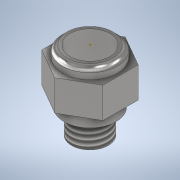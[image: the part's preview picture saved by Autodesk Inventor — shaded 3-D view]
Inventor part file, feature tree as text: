
AUTODESK INVENTOR PART (.ipt)
format: ipt  version: 2022 (Build 260153000, 153)  size: 174,592 bytes
history: native  units: mm
features: sketch x7, extrude x6, fillet x1, thread x1
ambient origin geometry x8: Origin, YZ Plane, XZ Plane, XY Plane, X Axis, Y Axis, Z Axis, Center Point
bodies: Solid1 (feature_tree)
feature tree (15):
  extrude  "Extrusion1"  Depth=8.0mm TaperAngle=0.0deg
  extrude  "Extrusion2"  Depth=4.0mm TaperAngle=0.0deg
  extrude  "Extrusion3"  Depth=10.0mm TaperAngle=0.0deg
  extrude  "Extrusion4"  Depth=13.0mm
  extrude  "Extrusion5"  Depth=1.5mm
  fillet  "Fillet1"  Radius=1.5mm
  extrude  "Extrusion6"  Depth=13.5mm TaperAngle=0.0deg
  thread  "Thread1"  [1 undecoded]
  sketch  "Sketch7"
  sketch  "Sketch1"  dims[d2=12.0mm d3=9.0mm d4=8.0mm d5=0.0mm]
  sketch  "Sketch2"  dims[d6=17.0mm d7=4.0mm d8=0.0mm]
  sketch  "Sketch3"  dims[d9=10.0mm d10=10.0mm d11=0.0mm]
  sketch  "Sketch4"  dims[d12=18.0mm d13=13.0mm]
  sketch  "Sketch5"  dims[d14=2.0mm d15=0.0mm d16=15.0mm d17=1.5mm d18=0.0mm]
  sketch  "Sketch6"  dims[d19=1.5mm d20=13.5mm d21=0.0mm d22=8.0mm d23=0.0mm]
note: 1 required parameter value undecoded (feature->parameter linkage not recoverable at this tier; creation-order binding heuristic only, values carry confidence <= 0.55)
